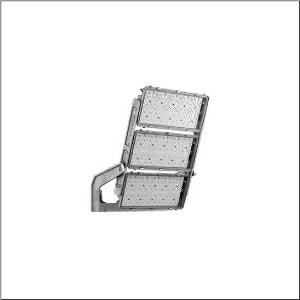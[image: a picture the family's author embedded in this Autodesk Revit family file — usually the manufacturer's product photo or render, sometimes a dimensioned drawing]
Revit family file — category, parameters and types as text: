
# Revit family: floodlight_fl_11_maxi_pro_remote___pl64_5xa779428v01aa_599d
name_source: partatom
category: Lighting Fixtures
units: mm (PartAtom-declared; Revit-internal decimal feet)

## family parameters
Cut with Voids When Loaded = No
Host = Face
Light Source = No
Part Type = Normal
Room Calculation Point = No
Round Connector Dimension = Use Diameter
Shared = No

## types (1)
- --- (1 x LED, 196240 lm, 1539.6 W, 5700K)
    Apparent Load = 1540 VA
    CIE Flux Codes = 28 79 98 100 100
    Color Rendering = 80
    Color Temperature = 5700K
    Default Elevation = 1800 mm
    Description = Floodlight FL 11  maxi  pro Remote floodlight; light control with lens of PMMA; cover panel of toughened safety glass, transparent; light distribution: PL64, asymmetric direct distribution, LEDcolour temperature: 5700K, rated luminous flux: 196.240lm, colour rendering: CRI > 80, light colour: 857; luminous efficacy: 128lm/W; brightness control: DALI 2 (1 DALI address); with terminal, 8-pole, max. 2.5mm², mains connection: 220..240V/380..400V AC, 50/60Hz, surge voltage resistance: line to ground: 10kV, dimming range 10..100%, dustproof LED module, LED unit replaceable without ESD environment, no afterglow with DALI off / DMX off command, ECG replaceable separately; 1540W floodlight with 3x LED unit of diecast aluminium, coated grey; length: 1.003mm / width: 651mm / height: 338mm; mounting bracket, of diecast aluminium, uncoated, natural, equipment: Power, protection rating (complete): IP66; insulation class (complete): insulation class I (protective earthing); certification: CE, ENEC, VDE; ball protection: ball impact resistant, impact resistance: IK07; only for outdoor installations, rated ambient temperature 10°C, permissible operating ambient temperature: -40..+30°C, permissible storage temperature: -40..+85°Cpackaging unit: 1 piece

Light Distribution: PL64
    Height = 320 mm
    Lamp = 1 x LED
    Lamp Light Flux = 196240 lm
    Lamp Power = 1539.6 W
    Lamp count = 1
    Length = 1002 mm
    Luminous efficacy = 127 lm/W
    Manufacturer = Siteco
    ModVariant = No
    Model = 5XA779428V01AA
    Mounting Place = Ceiling
    Mounting Type = Surface mounted
    Number of Poles = 1
    OnlyDefault = Yes
    Power Factor = 1
    Product Name = Floodlight FL 11 maxi pro Remote | PL64
    Product group = floodlight | ceiling mounted
    ProductGroupID = 301
    Protection Class = Protection class I
    Protection Degree = IP 66
    RLX_Detail_Level = 1
    RLX_Emergency_Light_Flux = 0 lm
    RLX_Emergency_Type = 0
    RLX_Emergency_Type_DB = No
    RlxData = <blob elided: 52381 chars, md5=fd0abc68>
    Socket = socket
    Standby Power = 0 W
    System Light Flux = 196240 lm
    System Power = 1540 W
    Type Comments = factory setting: luminous flux: 100 % | dim-lin: 254 | 1080 mA
    Type Image = l_1349141.jpg
    URL = http://relux.com
    VarID = @adj_102396
    Voltage = 0 V
    Weight = 0.00 kg
    Width = 655 mm

## geometry (parser evidence)
native form markers: Blend x4, Sweep x15
no freeform markers — native parametric forms only
